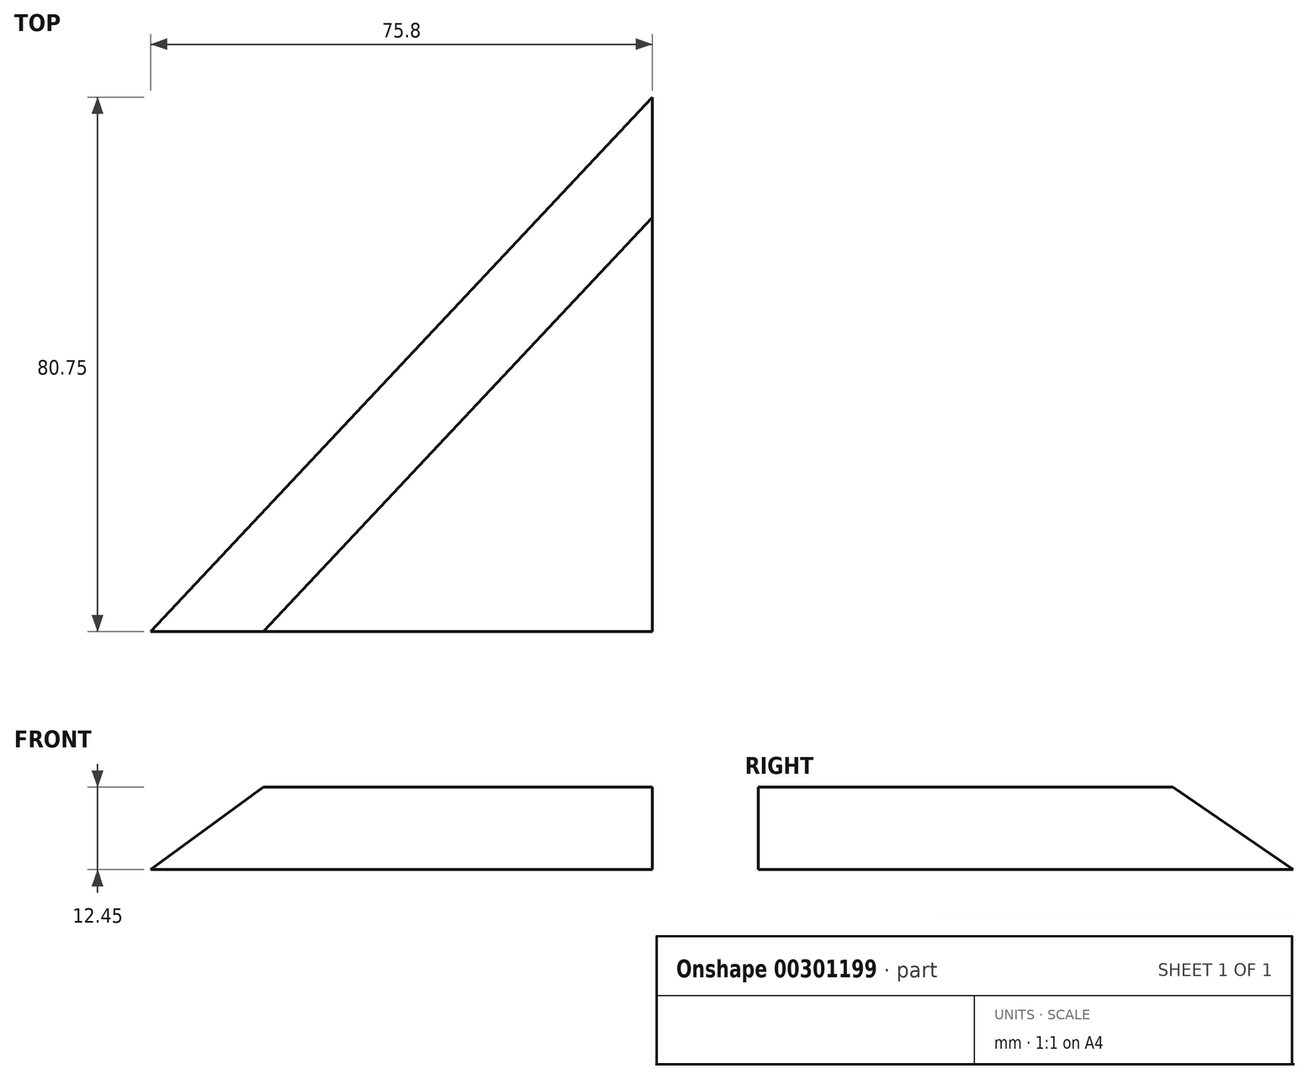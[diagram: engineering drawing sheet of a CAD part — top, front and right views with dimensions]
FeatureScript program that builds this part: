
annotation { "Feature Type Name" : "Feature", "Feature Type Description" : "" }
export const myFeature = defineFeature(function(context is Context, id is Id, definition is map)
    precondition{}
    {
        {
            var Q0;
            Q0=qCreatedBy(makeId("Top.planeOp"),FACE);
            var sketch = newSketch(context, id + "F0", { "sketchPlane" : qUnion([Q0])});
            skLineSegment(sketch, "E0.bottom", {"start": v(-76.09, -7.3) * mm, "end": v(77, -7.3) * mm});
            skLineSegment(sketch, "E0.top", {"start": v(-76.09, 29.22) * mm, "end": v(77, 29.22) * mm});
            skLineSegment(sketch, "E0.left", {"start": v(-76.09, -7.3) * mm, "end": v(-76.09, 29.22) * mm});
            skLineSegment(sketch, "E0.right", {"start": v(77, -7.3) * mm, "end": v(77, 29.22) * mm});
            skSolve(sketch);
        }
        {
            var Q0;
            Q0=makeQuery(id+"F0.imprint","IMPRINT",FACE,{"disambiguationData":[TD([[makeQuery(id+"F0.imprint","IMPRINT",EDGE,{"derivedFrom":sQuery(id+"F0.wireOp",EDGE,"E0.bottom")}),1.0]])]});
            var sketch = newSketch(context, id + "F1", { "sketchPlane" : qUnion([Q0])});
            skLineSegment(sketch, "E1", {"start": v(0, 29.41) * mm, "end": v(-75.8, 29.41) * mm});
            skLineSegment(sketch, "E2", {"start": v(-75.8, 29.41) * mm, "end": v(0, 110.16) * mm});
            skLineSegment(sketch, "E3", {"start": v(0, 110.16) * mm, "end": v(0, 29.41) * mm});
            skSolve(sketch);
        }
        {
            var Q0;
            Q0=makeQuery(id+"F1.imprint","IMPRINT",FACE,{"disambiguationData":[TD([[makeQuery(id+"F1.imprint","IMPRINT",EDGE,{"derivedFrom":sQuery(id+"F1.wireOp",EDGE,"E1")}),-1.0]])]});
            extrude(context, id + "F2", {"entities" : qUnion([Q0]), "depth" : 12.45 * mm});
        }
        {
            var Q0;
            Q0=makeQuery(id+"F2.opExtrude","CAP_EDGE",EDGE,{"disambiguationData":[OSD([sQuery(id+"F1.wireOp",EDGE,"E2")])],"isStart":false});
            chamfer(context, id + "F3", {"entities" : qUnion([Q0]), "width" : 12.45 * mm, "tangentPropagation" : true});
        }
    });
